# Revit family: IS_Conca_T3955_BIM_IT
name_source: partatom
category: Plumbing Fixtures
revit_build: Autodesk Revit 2017 (Build: 20160225_1515(x64)
units: mm (PartAtom-declared; Revit-internal decimal feet)

## family parameters
Always vertical = No
Cut with Voids When Loaded = No
OmniClass Number = 23.45.05.14.21.11
OmniClass Title = Bath/Shower Units
Part Type = Normal
Room Calculation Point = No
Round Connector Dimension = Use Diameter
Shared = No
Work Plane-Based = No

## types (6) — shared parameters
Accessori = https://www.idealstandard.it
Aiuto = https://www.idealstandard.it
AltezzaNominale = 1701 mm
Autore = Ideal Standard
BIMobject category = Storage
BIMobject category code = sanitary-storage
BIMobject main category = Sanitary
BIMobject main category code = sanitary
Brand = https://www.idealstandard.it
DescrizioneClassifcazioneUni2015 = Bathroom cabinets
DurataGaranzia = 2
DurataGaranziaProdotti = 2
Forma = Rettangolare
Garanzia = Garanzia Idealstandard
IfcEsportaCome = IfcFurnitureType
InformaziniGaranzia = https://www.idealstandard.it
InformazioniDiProdotto = http://www.idealstandard.it
InformazioniGaranzia = https://www.idealstandard.it
Installation instructions = https://www.idealspec.co.uk
InstruzioniInstallazione = https://www.idealstandard.it
LarghezzaNominale = 367 mm
Maniglia = No
Manufacturer = Ideal Standard
Materiale = Ceramics
NominalDepth = 250 mm  [stored 0.82021 ft]
NominalHeight = 1701 mm
NominalWidth = 367 mm
PesoNetto = 34
PiattoDoccia = No
Product group = Bathroom_Furniture
Produttore = Ideal Standard
ProfonditaNominale = 250 mm  [stored 0.82021 ft]
Revisione = 1
RiferimentoClassificazioneUni2015 = Pr_40_30_78_03
Spazio = Interno
Telefono = 800 652 290
TipoEspotazioneIfc = Bathroom cabinets
URL = https://www.ideal-standard.co.uk
Uniclass 2015 Code = Pr_40_30_78_03
Uniclass 2015 Name = Bathroom cabinets
UnitàDurata = Anno
UnitàDurataGaranzia = Anno
UnitàLineare = Milimitre
UnitàMonetaria = €
UnitàSuperficie = Milimitre
UnitàVolume = Litri
Versione = 1
VersioneClassificazioneUni2015 = v1.1
zero-valued in all types: CostoDiSostituzione, DimensioneScarico, LunghezzaNominale, Nominal depth, Nominal height, SeatMaterial, SpessoreDelMateriale, SpilloverLivello, Weight Net (Kg)

## per-type parameters (varying)
| type | Caratteristiche | CodiceABarre | CodiceArticolo | Colore | Description | Desrizione | Finitura | Model | ModelloDiRiferimento | Nome | NomeOggettoBim | NumeroDiModello |
| T3955Y1 - Conca COLUMN  WHMT - T3955 - Y1_MattWhite | Colonna 370x250x1700mm dotata di una porta reversibile con sistema di chiusura rallentata e apertura push to open. Dotata di 5 ripiani fissi.Finitura Bianco laccato opaco | 8014140461630 | T3955Y1 | Matt white | Column 370x250x1700mm equipped with a reversible door with slow closing system and push to open opening. Equipped with 5 fixed shelves. Matt white lacquered finish | Colonna 370x250x1700mm dotata di una porta reversibile con sistema di chiusura rallentata e apertura push to open. Dotata di 5 ripiani fissi.Finitura Bianco laccato opaco | Matt white | T3955Y1 | T3955Y1 | BathroomCabinets_Conca_T3955Y1_IdealStandard | ISI_IdealStandard_Bathroom Cabinets_Conca_T3955Y1 | T3955Y1 |
| T3955Y2 - Conca COLUMN  WHMT - T3955 - Y2_MattAntracite | Colonna 370x250x1700mm dotata di una porta reversibile con sistema di chiusura rallentata e apertura push to open. Dotata di 5 ripiani fissi. Finitura Antracite laccato opaco | 8014140461647 | T3955Y2 | Matt anthracite | Column 370x250x1700mm equipped with a reversible door with slow closing system and push to open opening. Equipped with 5 fixed shelves. Anthracite matt lacquer finish | Colonna 370x250x1700mm dotata di una porta reversibile con sistema di chiusura rallentata e apertura push to open. Dotata di 5 ripiani fissi. Finitura Antracite laccato opaco | Matt anthracite | T3955Y2 | T3955Y2 | BathroomCabinets_Conca_T3955Y2_IdealStandard | ISI_IdealStandard_Bathroom Cabinets_Conca_T3955Y2 | T3955Y2 |
| T3955Y3 - Conca COLUMN  WHMT - T3955 - Y3_MattSunset | Colonna 370x250x1700mm dotata di una porta reversibile con sistema di chiusura rallentata e apertura push to open. Dotata di 5 ripiani fissi. Finitura Sunset laccato opaco | 8014140461654 | T3955Y3 | Matt Sunset | Column 370x250x1700mm equipped with a reversible door with slow closing system and push to open opening. Equipped with 5 fixed shelves. Sunset matt lacquer finish | Colonna 370x250x1700mm dotata di una porta reversibile con sistema di chiusura rallentata e apertura push to open. Dotata di 5 ripiani fissi. Finitura Sunset laccato opaco | Matt Sunset | T3955Y3 | T3955Y3 | BathroomCabinets_Conca_T3955Y3_IdealStandard | ISI_IdealStandard_Bathroom Cabinets_Conca_T3955Y3 | T3955Y3 |
| T3955Y4 - Conca COLUMN  WHMT - T3955 - Y4_SmokedOak | Colonna 370x250x1700mm dotata di una porta reversibile con sistema di chiusura rallentata e apertura push to open. Dotata di 5 ripiani fissi. Finitura Rovere affumicato scuro | 8014140461661 | T3955Y4 | Matt Sunset | Column 370x250x1700mm equipped with a reversible door with slow closing system and push to open opening. Equipped with 5 fixed shelves. Dark smoked oak finish | Colonna 370x250x1700mm dotata di una porta reversibile con sistema di chiusura rallentata e apertura push to open. Dotata di 5 ripiani fissi. Finitura Rovere affumicato scuro | Matt Sunset | T3955Y4 | T3955Y4 | BathroomCabinets_Conca_T3955Y4_IdealStandard | ISI_IdealStandard_Bathroom Cabinets_Conca_T3955Y4 | T3955Y4 |
| T3955Y5 - Conca COLUMN  WHMT - T3955 - Y5_DarkWalnut | Colonna 370x250x1700mm dotata di una porta reversibile con sistema di chiusura rallentata e apertura push to open. Dotata di 5 ripiani fissi. Finitura Noce scuro | 8014140461678 | T3955Y5 | Dark Walnut | Column 370x250x1700mm equipped with a reversible door with slow closing system and push to open opening. Equipped with 5 fixed shelves. Dark Walnut finish | Colonna 370x250x1700mm dotata di una porta reversibile con sistema di chiusura rallentata e apertura push to open. Dotata di 5 ripiani fissi. Finitura Noce scuro | Dark Walnut | T3955Y5 | T3955Y5 | BathroomCabinets_Conca_T3955Y5_IdealStandard | ISI_IdealStandard_Bathroom Cabinets_Conca_T3955Y5 | T3955Y5 |
| T3955Y6 - Conca COLUMN  WHMT - T3955 - Y6_LightOak | Colonna 370x250x1700mm dotata di una porta reversibile con sistema di chiusura rallentata e apertura push to open. Dotata di 5 ripiani fissi. Finitura Legno chiaro | 8014140461685 | T3955Y6 | Light Oak | Column 370x250x1700mm equipped with a reversible door with slow closing system and push to open opening. Equipped with 5 fixed shelves. Light wood finish | Colonna 370x250x1700mm dotata di una porta reversibile con sistema di chiusura rallentata e apertura push to open. Dotata di 5 ripiani fissi. Finitura Legno chiaro | Light Oak | T3955Y6 | T3955Y6 | BathroomCabinets_Conca_T3955Y6_IdealStandard | ISI_IdealStandard_Bathroom Cabinets_Conca_T3955Y6 | T3955Y6 |

note: [stored X ft] marks values corroborated as IEEE doubles in the binary element streams (Revit-internal decimal feet)

## geometry (parser evidence)
native form markers: Sweep x3
no freeform markers — native parametric forms only
